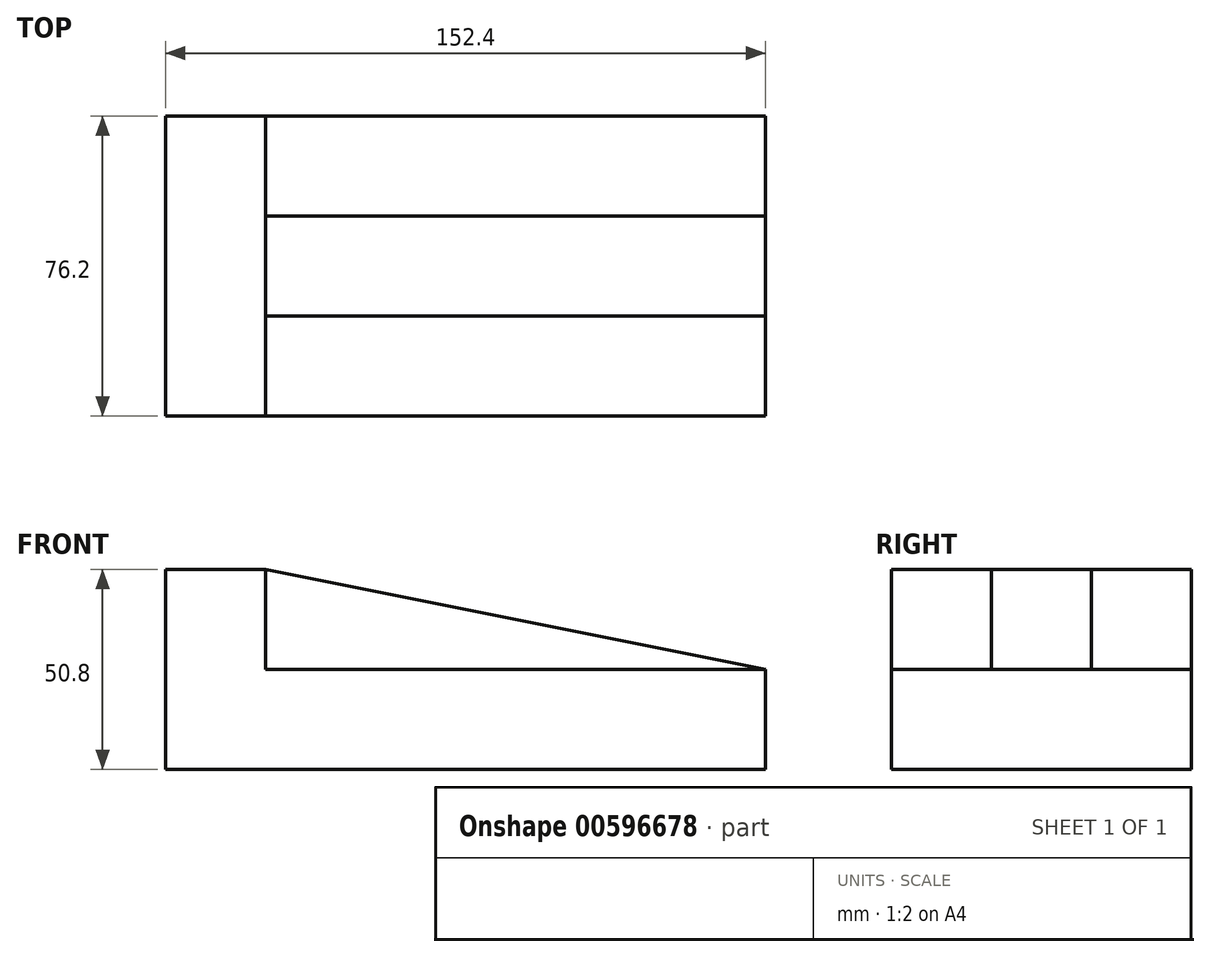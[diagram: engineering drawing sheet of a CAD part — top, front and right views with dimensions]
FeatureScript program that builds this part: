
annotation { "Feature Type Name" : "Feature", "Feature Type Description" : "" }
export const myFeature = defineFeature(function(context is Context, id is Id, definition is map)
    precondition{}
    {
        {
            var Q0;
            Q0=qCreatedBy(makeId("Front.planeOp"),FACE);
            var sketch = newSketch(context, id + "F0", { "sketchPlane" : qUnion([Q0])});
            skLineSegment(sketch, "E0.bottom", {"start": v(0, 0) * mm, "end": v(152.4, 0) * mm});
            skLineSegment(sketch, "E0.top", {"start": v(0, 25.4) * mm, "end": v(152.4, 25.4) * mm});
            skLineSegment(sketch, "E0.left", {"start": v(0, 0) * mm, "end": v(0, 25.4) * mm});
            skLineSegment(sketch, "E0.right", {"start": v(152.4, 0) * mm, "end": v(152.4, 25.4) * mm});
            skSolve(sketch);
        }
        {
            var Q0;
            Q0=makeQuery(id+"F0.imprint","IMPRINT",FACE,{"disambiguationData":[TD([[makeQuery(id+"F0.imprint","IMPRINT",EDGE,{"derivedFrom":sQuery(id+"F0.wireOp",EDGE,"E0.bottom")}),1.0]])]});
            extrude(context, id + "F1", {"entities" : qUnion([Q0]), "oppositeDirection" : true, "depth" : 76.2 * mm, "offsetDistance" : 25.4 * mm});
        }
        {
            var Q0;
            Q0=makeQuery(id+"F1.opExtrude","SWEPT_FACE",FACE,{"disambiguationData":[OSD([sQuery(id+"F0.wireOp",EDGE,"E0.top")])]});
            var sketch = newSketch(context, id + "F2", { "sketchPlane" : qUnion([Q0])});
            skLineSegment(sketch, "E1.bottom", {"start": v(0, 0) * mm, "end": v(25.4, 0) * mm});
            skLineSegment(sketch, "E1.top", {"start": v(0, 76.2) * mm, "end": v(25.4, 76.2) * mm});
            skLineSegment(sketch, "E1.left", {"start": v(0, 0) * mm, "end": v(0, 76.2) * mm});
            skLineSegment(sketch, "E1.right", {"start": v(25.4, 0) * mm, "end": v(25.4, 76.2) * mm});
            skSolve(sketch);
        }
        {
            var Q0;
            Q0=makeQuery(id+"F2.imprint","IMPRINT",FACE,{"disambiguationData":[TD([[makeQuery(id+"F2.imprint","IMPRINT",EDGE,{"derivedFrom":sQuery(id+"F2.wireOp",EDGE,"E1.bottom")}),1.0]])]});
            extrude(context, id + "F3", {"entities" : qUnion([Q0]), "operationType" : NewBodyOperationType.ADD, "depth" : 25.4 * mm, "offsetDistance" : 25.4 * mm});
        }
        {
            var Q0;
            Q0=makeQuery(id+"F1.opExtrude","SWEPT_FACE",FACE,{"disambiguationData":[OSD([sQuery(id+"F0.wireOp",EDGE,"E0.top")])]});
            var sketch = newSketch(context, id + "F4", { "sketchPlane" : qUnion([Q0])});
            skLineSegment(sketch, "E2", {"start": v(25.4, 50.8) * mm, "end": v(152.4, 50.8) * mm});
            skLineSegment(sketch, "E3", {"start": v(152.4, 50.8) * mm, "end": v(152.4, 25.4) * mm});
            skLineSegment(sketch, "E4", {"start": v(152.4, 25.4) * mm, "end": v(25.4, 25.4) * mm});
            skLineSegment(sketch, "E5", {"start": v(25.4, 25.4) * mm, "end": v(25.4, 50.8) * mm});
            skSolve(sketch);
        }
        {
            var Q0;
            Q0=makeQuery(id+"F4.imprint","IMPRINT",FACE,{"disambiguationData":[TD([[makeQuery(id+"F4.imprint","IMPRINT",EDGE,{"derivedFrom":sQuery(id+"F4.wireOp",EDGE,"E2")}),-1.0]])]});
            extrude(context, id + "F5", {"entities" : qUnion([Q0]), "operationType" : NewBodyOperationType.ADD, "depth" : 25.4 * mm, "offsetDistance" : 25.4 * mm});
        }
        {
            var Q0;
            Q0=makeQuery(id+"F5.opExtrude","SWEPT_FACE",FACE,{"disambiguationData":[OSD([sQuery(id+"F4.wireOp",EDGE,"E4")])]});
            var sketch = newSketch(context, id + "F6", { "sketchPlane" : qUnion([Q0])});
            skLineSegment(sketch, "E6", {"start": v(25.4, 50.8) * mm, "end": v(25.4, 25.4) * mm});
            skLineSegment(sketch, "E7", {"start": v(25.4, 25.4) * mm, "end": v(152.4, 25.4) * mm});
            skLineSegment(sketch, "E8", {"start": v(152.4, 25.4) * mm, "end": v(25.4, 50.8) * mm});
            skSolve(sketch);
        }
        {
            var Q0;
            Q0=makeQuery(id+"F6.imprint","IMPRINT",FACE,{"disambiguationData":[TD([[makeQuery(id+"F6.imprint","IMPRINT",EDGE,{"derivedFrom":sQuery(id+"F6.wireOp",EDGE,"E8")}),-1.0]])]});
            extrude(context, id + "F7", {"entities" : qUnion([Q0]), "operationType" : NewBodyOperationType.REMOVE, "oppositeDirection" : true, "depth" : 25.4 * mm, "offsetDistance" : 25.4 * mm});
        }
    });
